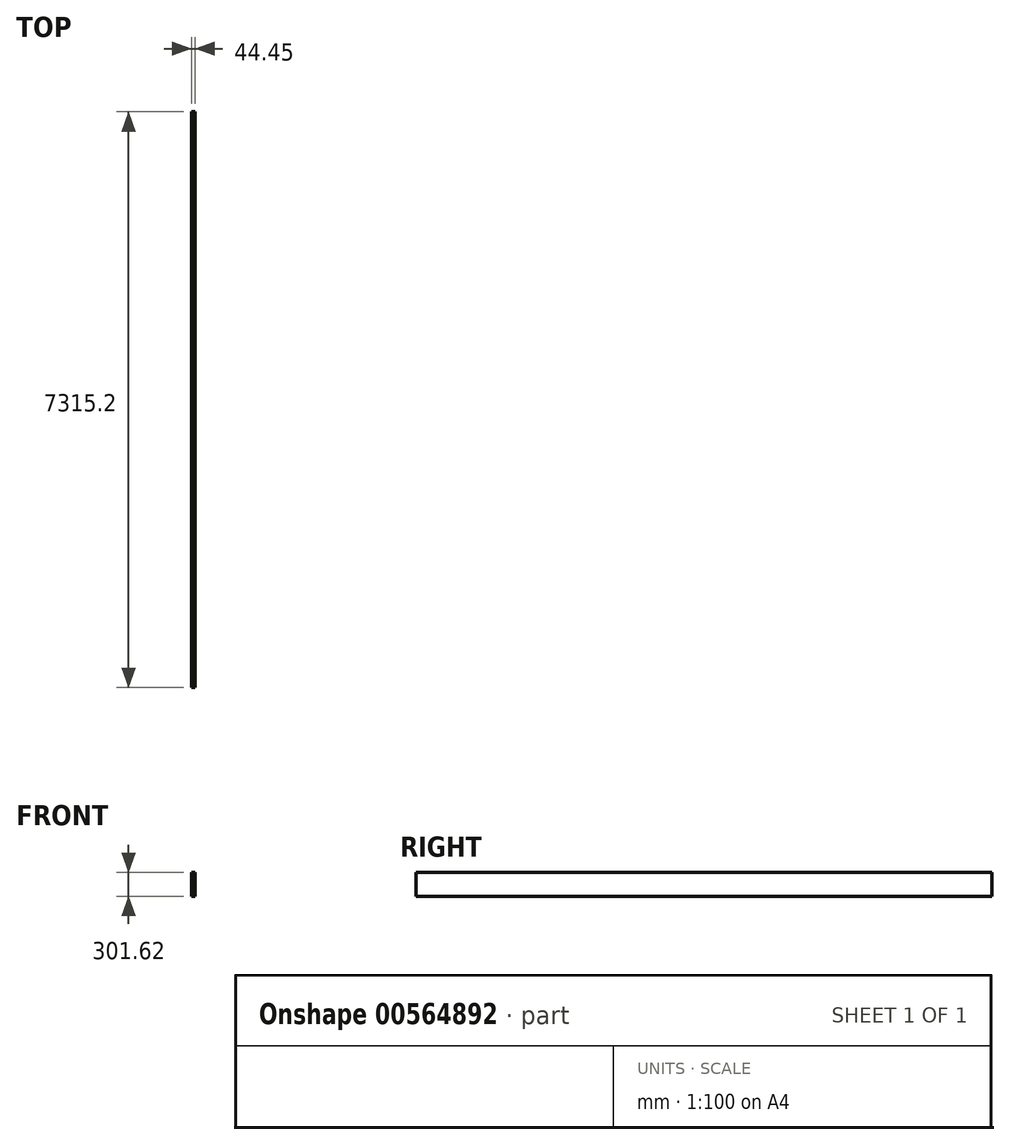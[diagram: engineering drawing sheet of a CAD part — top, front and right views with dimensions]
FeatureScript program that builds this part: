
annotation { "Feature Type Name" : "Feature", "Feature Type Description" : "" }
export const myFeature = defineFeature(function(context is Context, id is Id, definition is map)
    precondition{}
    {
        {
            var Q0;
            Q0=qCreatedBy(makeId("Front.planeOp"),FACE);
            var sketch = newSketch(context, id + "F0", { "sketchPlane" : qUnion([Q0])});
            skLineSegment(sketch, "E0.bottom", {"start": v(0, 0) * mm, "end": v(44.45, 0) * mm});
            skLineSegment(sketch, "E0.top", {"start": v(0, 301.63) * mm, "end": v(44.45, 301.63) * mm});
            skLineSegment(sketch, "E0.left", {"start": v(0, 0) * mm, "end": v(0, 301.63) * mm});
            skLineSegment(sketch, "E0.right", {"start": v(44.45, 0) * mm, "end": v(44.45, 301.63) * mm});
            skSolve(sketch);
        }
        {
            var Q0;
            Q0=qSketchRegion(id+"F0",true);
            extrude(context, id + "F1", {"entities" : qUnion([Q0]), "depth" : 7315.2 * mm, "offsetDistance" : 25.4 * mm});
        }
    });
